# Revit family: Gleitlager T HV1, m.D., Ø64 bis Ø219mm (h=101mm bis 127mm)
name_source: partatom
category: HLS-Bauteile
revit_build: Autodesk Revit 2018 (Build: 20190510_1515(x64)
units: mm (PartAtom-declared; Revit-internal decimal feet)

## family parameters
Arbeitsebenenbasiert = Ja
Beim Laden mit Abzugskörper schneiden = Nein
Bemaßung runder Anschluss = Durchmesser verwenden
Gemeinsam genutzt = Ja
Immer vertikal = Nein
Klassifizierung = Keine
Raumberechnungspunkt = Nein
Teiletyp = Normal

## types (13) — shared parameters
Anzahl Rohrschellen = 2
Baustoffklasse = B2
Breite Schellenband = 50 mm
Breite Unterbau = 100 mm
Dämmstärke = 6 mm  [stored 0.019685 ft]
Fabrikat = MEFA
Firma = MEFA Befestigungs- und Montagesysteme GmbH
Hersteller = MEFA
Kurztext1 = Gleitlager T 2 RS HV1 50x5
Länge Unterbau = 250 mm
Mengeneinheit = St
Schalldämmeinlage = Gummi EPDM
Sicherheitsfaktor = 1.54
Stärke Material = 8 mm  [stored 0.0262467 ft]
Stärke Schellenband = 5 mm
Verschluss = Mutter / Verschluss-Schraube
Vorgabe-Ansicht = 1219 mm
max. Höhe Unterbau = 125 mm
max. Temperaturbeständigkeit = 100 °C
min. Höhe Unterbau = 100 mm
vpe = 1
zero-valued in all types: max. Rohraußendurchmesser, min. Rohraußendurchmesser

## per-type parameters (varying)
| type | Artikelnummer | EAN | Gewicht | Gewicht pro Bauteil | Kurztext2 | Schellenteil | max. Rohrachse | min. Rohrachse |
| Typ HV1, m. 2 RS, m.D., Ø64mm (h=101 bis 127mm) | 141afbb0064 | 4250928461001 | 5.14 kg | 5.14 kg | 64 mm EPDM 100x250 mm fsv | TL-141S_b0076 bis 0231, m.D : mit RS Ø64mm m.D | 159 mm | 133 mm |
| Typ HV1, m. 2 RS, m.D., Ø76mm (h=101 bis 127mm) | 141afbb0076 | 4250928461018 | 5.35 kg | 5.35 kg | 76 mm EPDM 100x250 mm fsv | TL-141S_b0076 bis 0231, m.D : mit RS Ø76mm m.D | 165 mm | 139 mm |
| Typ HV1, m. 2 RS, m.D., Ø89mm (h=101 bis 127mm) | 141afbb0089 | 4250928461025 | 5.55 kg | 5.55 kg | 89 mm EPDM 100x250 mm fsv | TL-141S_b0076 bis 0231, m.D : mit RS Ø88.9mm, m.D | 172 mm | 146 mm |
| Typ HV1, m. 2 RS, m.D., Ø108mm (h=101 bis 127mm) | 141afbb0108 | 4250928461032 | 5.85 kg | 5.85 kg | 108 mm EPDM 100x250 mm fsv | TL-141S_b0076 bis 0231, m.D : mit RS Ø108mm m.D | 181 mm | 155 mm |
| Typ HV1, m. 2 RS, m.D., Ø110mm (h=101 bis 127mm) | 141afbb0110 | 4250928461049 | 5.89 kg | 5.89 kg | 110 mm EPDM 100x250 mm fsv | TL-141S_b0076 bis 0231, m.D : mit RS Ø110mm m.D | 182 mm | 156 mm |
| Typ HV1, m. 2 RS, m.D., Ø133mm (h=101 bis 127mm) | 141afbb0133 | 4250928461063 | 6.25 kg | 6.25 kg | 133 mm EPDM 100x250 mm fsv | TL-141S_b0076 bis 0231, m.D : mit RS Ø133mm m.D | 194 mm | 168 mm |
| Typ HV1, m. 2 RS, m.D., Ø114mm (h=101 bis 127mm) | 141afbb0114 | 4250928461056 | 5.95 kg | 5.95 kg | 114 mm EPDM 100x250 mm fsv | TL-141S_b0076 bis 0231, m.D : mit RS Ø114.3mm m.D | 184 mm | 158 mm |
| Typ HV1, m. 2 RS, m.D., Ø140mm (h=101 bis 127mm) | 141afbb0140 | 4250928461070 | 6.37 kg | 6.37 kg | 140 mm EPDM 100x250 mm fsv | TL-141S_b0076 bis 0231, m.D : mit RS Ø139.7mm m.D | 197 mm | 171 mm |
| Typ HV1, m. 2 RS, m.D., Ø160mm (h=101 bis 127mm) | 141afbb0160 | 4250928461087 | 6.69 kg | 6.69 kg | 160 mm EPDM 100x250 mm fsv | TL-141S_b0076 bis 0231, m.D : mit RS Ø160mm m.D | 207 mm | 181 mm |
| Typ HV1, m. 2 RS, m.D., Ø168mm (h=101 bis 127mm) | 141afbb0168 | 4250928461094 | 6.82 kg | 6.82 kg | 168 mm EPDM 100x250 mm fsv | TL-141S_b0076 bis 0231, m.D : mit RS Ø168.3mm m.D | 211 mm | 185 mm |
| Typ HV1, m. 2 RS, m.D., Ø180mm (h=101 bis 127mm) | 141afbb0180 | 4250928461100 | 7.01 kg | 7.01 kg | 180 mm EPDM 100x250 mm fsv | TL-141S_b0076 bis 0231, m.D : mit RS Ø180mm m.D | 217 mm | 191 mm |
| Typ HV1, m. 2 RS, m.D., Ø210mm (h=101 bis 127mm) | 141afbb0210 | 4250928461117 | 7.49 kg | 7.49 kg | 210 mm EPDM 100x250 mm fsv | TL-141S_b0076 bis 0231, m.D : mit RS Ø210mm m.D | 232 mm | 206 mm |
| Typ HV1, m. 2 RS, m.D., Ø219mm (h=101 bis 127mm) | 141afbb0219 | 4250928461124 | 7.63 kg | 7.63 kg | 219 mm EPDM 100x250 mm fsv | TL-141S_b0076 bis 0231, m.D : mit RS Ø219mm m.D | 237 mm | 211 mm |

note: [stored X ft] marks values corroborated as IEEE doubles in the binary element streams (Revit-internal decimal feet)

## geometry (parser evidence)
native form markers: Sweep x9
no freeform markers — native parametric forms only
